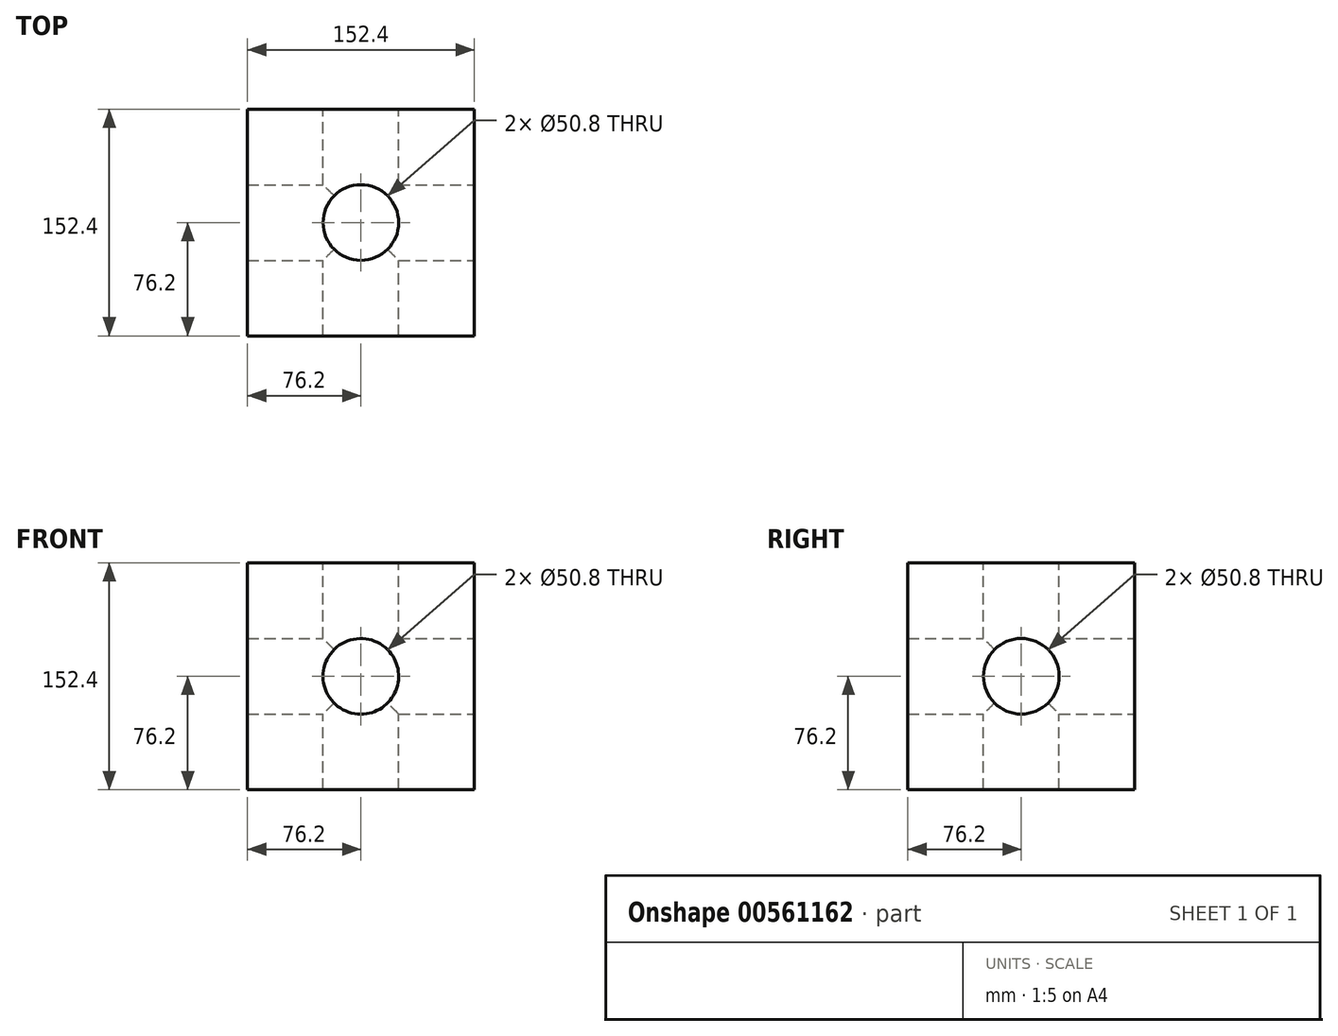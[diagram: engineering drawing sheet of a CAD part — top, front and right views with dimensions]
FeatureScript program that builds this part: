
annotation { "Feature Type Name" : "Feature", "Feature Type Description" : "" }
export const myFeature = defineFeature(function(context is Context, id is Id, definition is map)
    precondition{}
    {
        {
            var Q0;
            Q0=qCreatedBy(makeId("Top.planeOp"),FACE);
            var sketch = newSketch(context, id + "F0", { "sketchPlane" : qUnion([Q0])});
            skLineSegment(sketch, "E0.bottom", {"start": v(76.2, -76.2) * mm, "end": v(-76.2, -76.2) * mm});
            skLineSegment(sketch, "E0.top", {"start": v(76.2, 76.2) * mm, "end": v(-76.2, 76.2) * mm});
            skLineSegment(sketch, "E0.left", {"start": v(76.2, -76.2) * mm, "end": v(76.2, 76.2) * mm});
            skLineSegment(sketch, "E0.right", {"start": v(-76.2, -76.2) * mm, "end": v(-76.2, 76.2) * mm});
            skPoint(sketch, "E0.middle", {"position": v(0, 0) * mm});
            skSolve(sketch);
        }
        {
            var Q0;
            Q0 = qSketchRegion(id + "F0", true);
            extrude(context, id + "F1", {"entities" : qUnion([Q0]), "depth" : 152.4 * mm, "offsetDistance" : 25.4 * mm});
        }
        {
            var Q0;
            Q0=makeQuery(id+"F1.opExtrude","SWEPT_FACE",FACE,{"disambiguationData":[OSD([sQuery(id+"F0.wireOp",EDGE,"E0.left")])]});
            var sketch = newSketch(context, id + "F2", { "sketchPlane" : qUnion([Q0])});
            skCircle(sketch, "E1", {"center": v(0, 76.2) * mm, "radius": 25.4 * mm});
            skPoint(sketch, "E1.centerSnap0", {"position": v(-76.2, 76.2) * mm});
            skPoint(sketch, "E1.centerSnap1", {"position": v(0, 0) * mm});
            skSolve(sketch);
        }
        {
            var Q0;
            Q0 = qSketchRegion(id + "F2", true);
            extrude(context, id + "F3", {"entities" : qUnion([Q0]), "operationType" : NewBodyOperationType.REMOVE, "endBound" : BoundingType.THROUGH_ALL, "oppositeDirection" : true, "depth" : 152.4 * mm, "offsetDistance" : 25.4 * mm});
        }
        {
            var Q0;
            Q0=makeQuery(id+"F1.opExtrude","SWEPT_FACE",FACE,{"disambiguationData":[OSD([sQuery(id+"F0.wireOp",EDGE,"E0.top")])]});
            var sketch = newSketch(context, id + "F4", { "sketchPlane" : qUnion([Q0])});
            skCircle(sketch, "E2", {"center": v(0, 76.2) * mm, "radius": 25.4 * mm});
            skPoint(sketch, "E2.centerSnap0", {"position": v(-76.2, 76.2) * mm});
            skSolve(sketch);
        }
        {
            var Q0;
            Q0 = qSketchRegion(id + "F4", true);
            extrude(context, id + "F5", {"entities" : qUnion([Q0]), "operationType" : NewBodyOperationType.REMOVE, "endBound" : BoundingType.THROUGH_ALL, "oppositeDirection" : true, "depth" : 152.4 * mm, "offsetDistance" : 25.4 * mm});
        }
        {
            var Q0;
            Q0=makeQuery(id+"F1.opExtrude","CAP_FACE",FACE,{"disambiguationData":[OSD([sQuery(id+"F0.wireOp",EDGE,"E0.bottom"),sQuery(id+"F0.wireOp",EDGE,"E0.top"),sQuery(id+"F0.wireOp",EDGE,"E0.left"),sQuery(id+"F0.wireOp",EDGE,"E0.right")])],"isStart":false});
            var sketch = newSketch(context, id + "F6", { "sketchPlane" : qUnion([Q0])});
            skCircle(sketch, "E3", {"center": v(0, 0) * mm, "radius": 25.4 * mm});
            skSolve(sketch);
        }
        {
            var Q0;
            Q0 = qSketchRegion(id + "F6", true);
            extrude(context, id + "F7", {"entities" : qUnion([Q0]), "operationType" : NewBodyOperationType.REMOVE, "endBound" : BoundingType.THROUGH_ALL, "oppositeDirection" : true, "depth" : 152.4 * mm, "offsetDistance" : 25.4 * mm});
        }
    });
